FCSTD DOCUMENT  (FreeCAD 1.0R39109 (Git))
Label: caja
License: All rights reserved
LicenseURL: https://en.wikipedia.org/wiki/All_rights_reserved
objects: Sketcher::SketchObject×1, PartDesign::Pad×1, PartDesign::Body×1
note: 6 computed .brp shape members not serialized (recipe doc carries the construction recipe); baked Part::Feature solids carry a one-line shape summary decoded from their .brp

FEATURE [Sketcher::SketchObject] Sketch
  ArcFitTolerance = 1e-06
  AttachmentSupport = -> [XZ_Plane]
  FullyConstrained = false
  MakeInternals = false
  MapMode = 5
  Placement = pos=(0,0,0) rot=(1,0,0;1.5708rad)
  sketch-geometry (13):
    g0: LineSegment StartX=0 StartY=0 StartZ=0 EndX=0 EndY=100 EndZ=0
    g1: LineSegment StartX=0 StartY=100 StartZ=0 EndX=-80 EndY=100 EndZ=0
    g2: LineSegment StartX=-80 StartY=100 StartZ=0 EndX=-80 EndY=0 EndZ=0
    g3: LineSegment StartX=-80 StartY=0 StartZ=0 EndX=0 EndY=0 EndZ=0
    g4: LineSegment StartX=-10 StartY=10 StartZ=0 EndX=-10 EndY=90 EndZ=0
    g5: LineSegment StartX=-10 StartY=90 StartZ=0 EndX=-70 EndY=90 EndZ=0
    g6: LineSegment StartX=-70 StartY=90 StartZ=0 EndX=-70 EndY=10 EndZ=0
    g7: LineSegment StartX=-70 StartY=10 StartZ=0 EndX=-10 EndY=10 EndZ=0
    g8: LineSegment StartX=-70 StartY=10 StartZ=0 EndX=-35 EndY=10 EndZ=0
    g9: LineSegment StartX=-35 StartY=10 StartZ=0 EndX=-35 EndY=55 EndZ=0
    g10: LineSegment StartX=-70 StartY=55 StartZ=0 EndX=-70 EndY=10 EndZ=0
    g11: ArcOfCircle CenterX=-35 CenterY=10 CenterZ=0 NormalX=0 NormalY=0 NormalZ=1 AngleXU=0 Radius=45 StartAngle=1.5708 EndAngle=2.46192
    g12: ArcOfCircle CenterX=-35 CenterY=10 CenterZ=0 NormalX=0 NormalY=0 NormalZ=1 AngleXU=0 Radius=45 StartAngle=3.14159 EndAngle=3.14159
  constraints (35):
    c: Coincident(g0,g1)
    c: Coincident(g1,g2)
    c: Coincident(g2,g3)
    c: Coincident(g3,g0)
    c: Vertical(g0)
    c: Vertical(g2)
    c: Horizontal(g1)
    c: Horizontal(g3)
    c: Distance(g0,g2) = 80
    c: Distance(g1,g3) = 100
    c: Coincident(g0,g-1)
    c: Coincident(g4,g5)
    c: Coincident(g5,g6)
    c: Coincident(g6,g7)
    c: Coincident(g7,g4)
    c: Vertical(g4)
    c: Vertical(g6)
    c: Horizontal(g5)
    c: Horizontal(g7)
    c: Distance(g1,g5) = 10
    c: Distance(g0,g4) = 10
    c: Distance(g2,g6) = 10
    c: Distance(g3,g7) = 10
    c: Coincident(g8,g9)
    c: Coincident(g10,g8)
    c: Horizontal(g8)
    c: Vertical(g9)
    c: Vertical(g10)
    c: Distance(g9,g10) = 35
    c: Distance(g8,g10) = 45
    c: Coincident(g8,g6)
    c: Equal(g11,g12)
    c: PointOnObject(g11,g6)
    c: PointOnObject(g12,g2)
    c: Coincident(g11,g12)
FEATURE [PartDesign::Pad] Pad
  Direction = (1,1,1)
  Length = 10
  Length2 = 10
  Profile = -> Sketch
  ReferenceAxis = -> Sketch [N_Axis]
  Refine = true
  Suppressed = false
  Type = 0
FEATURE [PartDesign::Body] Body  label="Cuerpo"
  AllowCompound = false
  Group = -> [Sketch,Pad]
  Origin = -> Origin
  Tip = -> Pad
